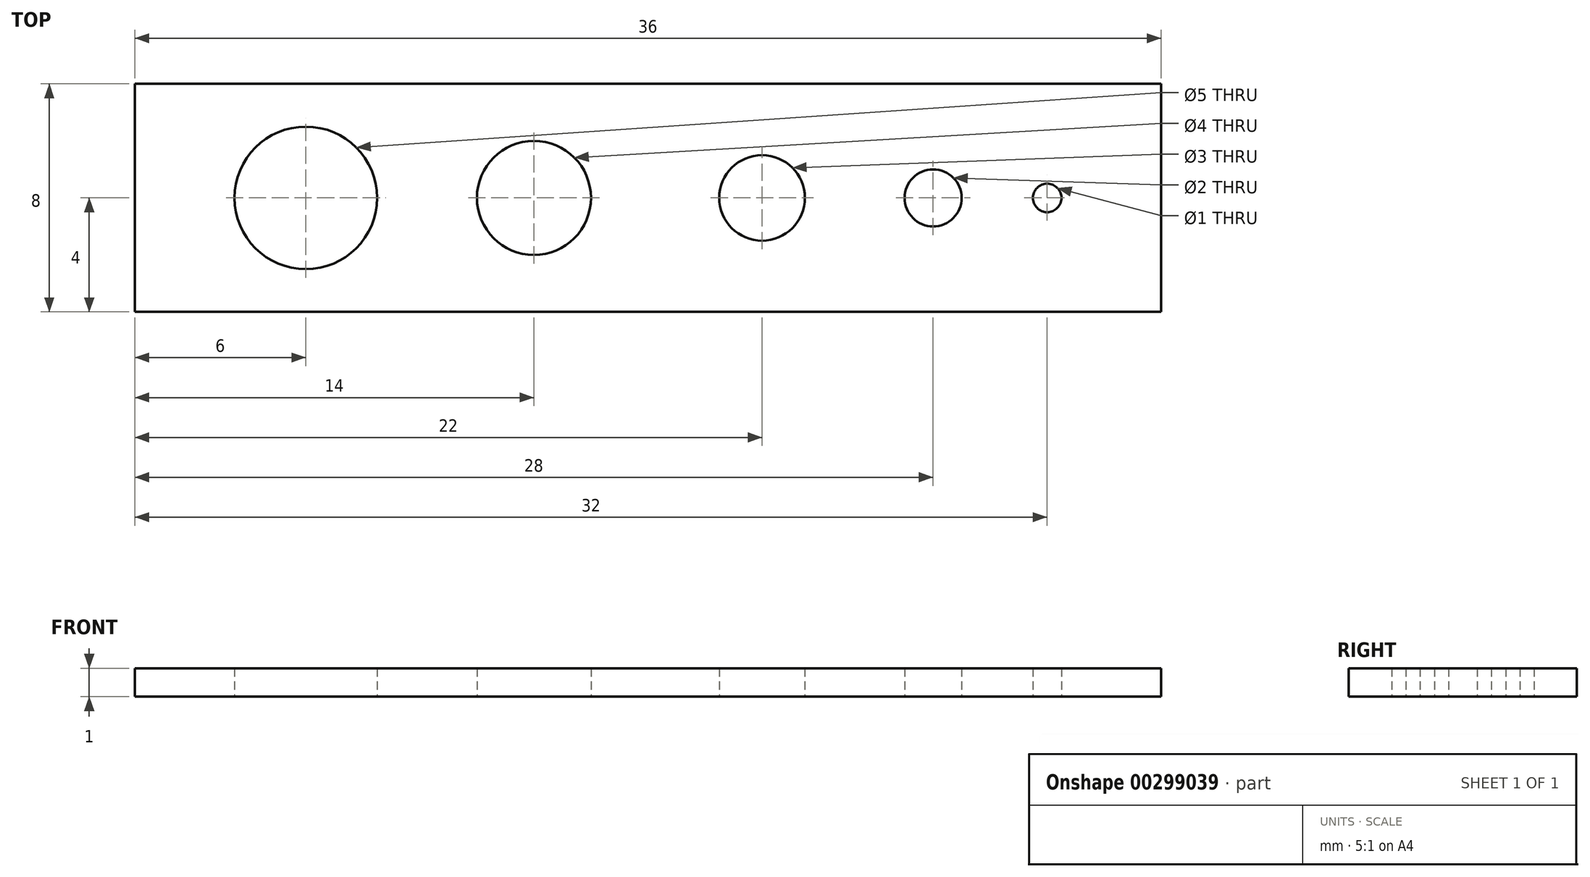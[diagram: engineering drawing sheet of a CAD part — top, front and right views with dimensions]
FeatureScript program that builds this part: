
annotation { "Feature Type Name" : "Feature", "Feature Type Description" : "" }
export const myFeature = defineFeature(function(context is Context, id is Id, definition is map)
    precondition{}
    {
        {
            var Q0;
            Q0=qCreatedBy(makeId("Top.planeOp"),FACE);
            var sketch = newSketch(context, id + "F0", { "sketchPlane" : qUnion([Q0])});
            skLineSegment(sketch, "E0.bottom", {"start": v(-22, 4) * mm, "end": v(14, 4) * mm});
            skLineSegment(sketch, "E0.top", {"start": v(-22, -4) * mm, "end": v(14, -4) * mm});
            skLineSegment(sketch, "E0.left", {"start": v(-22, 4) * mm, "end": v(-22, -4) * mm});
            skLineSegment(sketch, "E0.right", {"start": v(14, 4) * mm, "end": v(14, -4) * mm});
            skPoint(sketch, "E0.middle", {"position": v(0, 0) * mm});
            skCircle(sketch, "E1", {"center": v(-16, 0) * mm, "radius": 2.5 * mm});
            skCircle(sketch, "E2", {"center": v(-8, 0) * mm, "radius": 2 * mm});
            skCircle(sketch, "E3", {"center": v(0, 0) * mm, "radius": 1.5 * mm});
            skCircle(sketch, "E4", {"center": v(6, 0) * mm, "radius": 1 * mm});
            skCircle(sketch, "E5", {"center": v(10, 0) * mm, "radius": 0.5 * mm});
            skLineSegment(sketch, "E6", {"start": v(-16, 4) * mm, "end": v(-16, 0) * mm, "construction": true});
            skLineSegment(sketch, "E7", {"start": v(-16, -4) * mm, "end": v(-16, 0) * mm, "construction": true});
            skSolve(sketch);
        }
        {
            var Q0;
            Q0=makeQuery(id+"F0.imprint","IMPRINT",FACE,{"disambiguationData":[TD([[makeQuery(id+"F0.imprint","IMPRINT",EDGE,{"derivedFrom":sQuery(id+"F0.wireOp",EDGE,"E0.bottom")}),-1.0]])]});
            extrude(context, id + "F1", {"entities" : qUnion([Q0]), "depth" : 1 * mm});
        }
    });
